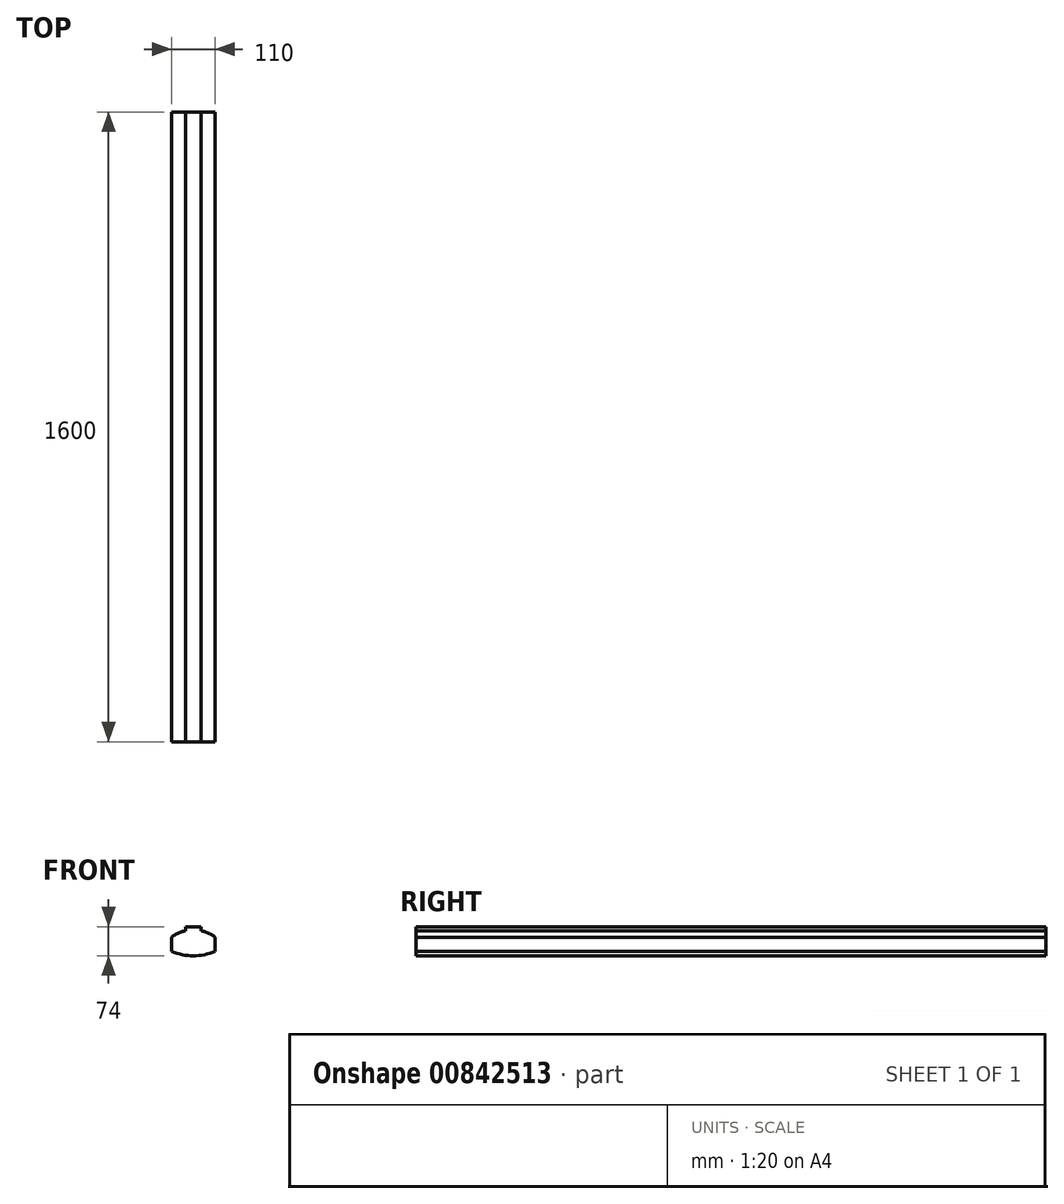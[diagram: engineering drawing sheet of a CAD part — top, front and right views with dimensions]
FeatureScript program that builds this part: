
annotation { "Feature Type Name" : "Feature", "Feature Type Description" : "" }
export const myFeature = defineFeature(function(context is Context, id is Id, definition is map)
    precondition{}
    {
        {
            var Q0;
            Q0=qCreatedBy(makeId("Front.planeOp"),FACE);
            var sketch = newSketch(context, id + "F0", { "sketchPlane" : qUnion([Q0])});
            skLineSegment(sketch, "E0.left", {"start": v(55, 17.72) * mm, "end": v(55, -17.72) * mm});
            skLineSegment(sketch, "E0.right", {"start": v(-55, 17.72) * mm, "end": v(-55, -17.72) * mm});
            skPoint(sketch, "E0.middle", {"position": v(0, 0) * mm});
            skArc(sketch, "E1", {"start": v(55, 17.72) * mm, "mid": v(38.4, 27.83) * mm, "end": v(20, 34.16) * mm});
            skArc(sketch, "E2", {"start": v(-55, -17.72) * mm, "mid": v(0, -29.84) * mm, "end": v(55, -17.72) * mm});
            skLineSegment(sketch, "E3.top", {"start": v(-20, 44.16) * mm, "end": v(20, 44.16) * mm});
            skLineSegment(sketch, "E3.left", {"start": v(-20, 34.16) * mm, "end": v(-20, 44.16) * mm});
            skLineSegment(sketch, "E3.right", {"start": v(20, 34.16) * mm, "end": v(20, 44.16) * mm});
            skArc(sketch, "E4.trimOffspring", {"start": v(-20, 34.16) * mm, "mid": v(-38.4, 27.83) * mm, "end": v(-55, 17.72) * mm});
            skSolve(sketch);
        }
        {
            var Q0;
            Q0 = qSketchRegion(id + "F0", true);
            extrude(context, id + "F1", {"entities" : qUnion([Q0]), "depth" : 1600 * mm, "offsetDistance" : 25 * mm});
        }
    });
